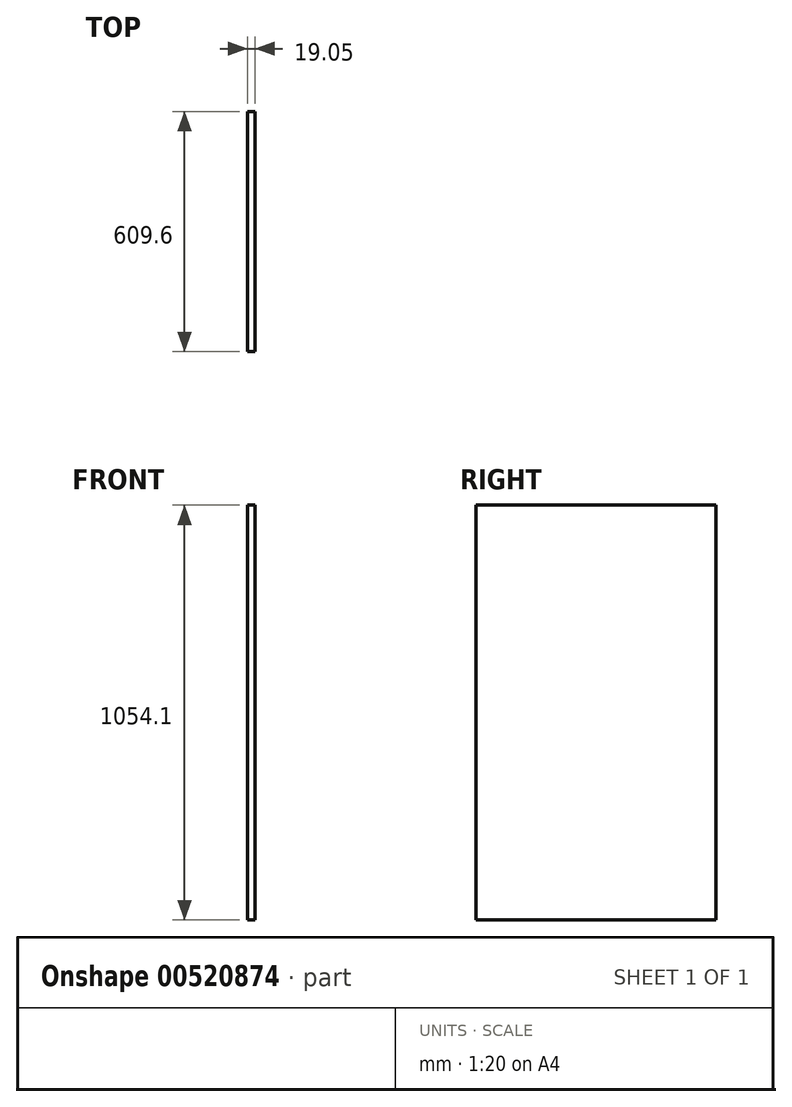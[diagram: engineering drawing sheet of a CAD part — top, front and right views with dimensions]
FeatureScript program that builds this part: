
annotation { "Feature Type Name" : "Feature", "Feature Type Description" : "" }
export const myFeature = defineFeature(function(context is Context, id is Id, definition is map)
    precondition{}
    {
        {
            var Q0;
            Q0=qCreatedBy(makeId("Right.planeOp"),FACE);
            var sketch = newSketch(context, id + "F0", { "sketchPlane" : qUnion([Q0])});
            skLineSegment(sketch, "E0.bottom", {"start": v(304.8, 527.05) * mm, "end": v(-304.8, 527.05) * mm});
            skLineSegment(sketch, "E0.top", {"start": v(304.8, -527.05) * mm, "end": v(-304.8, -527.05) * mm});
            skLineSegment(sketch, "E0.left", {"start": v(304.8, 527.05) * mm, "end": v(304.8, -527.05) * mm});
            skLineSegment(sketch, "E0.right", {"start": v(-304.8, 527.05) * mm, "end": v(-304.8, -527.05) * mm});
            skPoint(sketch, "E0.middle", {"position": v(0, 0) * mm});
            skSolve(sketch);
        }
        {
            var Q0;
            Q0=makeQuery(id+"F0.imprint","IMPRINT",FACE,{"disambiguationData":[TD([[makeQuery(id+"F0.imprint","IMPRINT",EDGE,{"derivedFrom":sQuery(id+"F0.wireOp",EDGE,"E0.bottom")}),1.0]])]});
            extrude(context, id + "F1", {"entities" : qUnion([Q0]), "depth" : 19.05 * mm, "offsetDistance" : 25.4 * mm});
        }
    });
